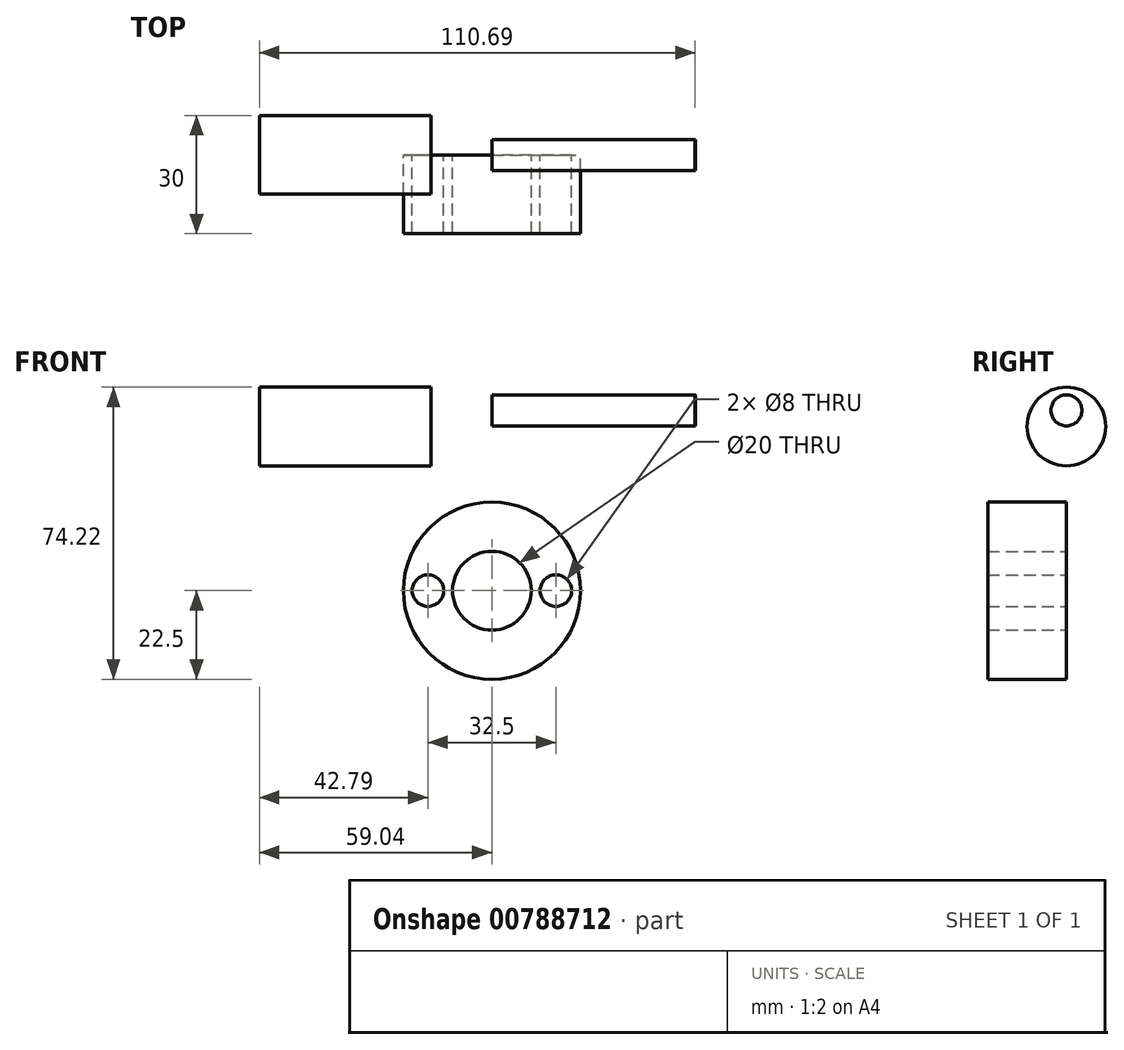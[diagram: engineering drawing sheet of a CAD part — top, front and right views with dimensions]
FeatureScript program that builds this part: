
annotation { "Feature Type Name" : "Feature", "Feature Type Description" : "" }
export const myFeature = defineFeature(function(context is Context, id is Id, definition is map)
    precondition{}
    {
        {
            var Q0;
            Q0=qCreatedBy(makeId("Front.planeOp"),FACE);
            var sketch = newSketch(context, id + "F0", { "sketchPlane" : qUnion([Q0])});
            skCircle(sketch, "E0", {"center": v(0, 0) * mm, "radius": 22.5 * mm});
            skCircle(sketch, "E1", {"center": v(0, 0) * mm, "radius": 10 * mm});
            skCircle(sketch, "E2", {"center": v(16.25, 0) * mm, "radius": 6.25 * mm});
            skCircle(sketch, "E3", {"center": v(-16.25, 0) * mm, "radius": 6.25 * mm});
            skCircle(sketch, "E4", {"center": v(-16.25, 0) * mm, "radius": 4 * mm});
            skCircle(sketch, "E5", {"center": v(16.25, 0) * mm, "radius": 4 * mm});
            skSolve(sketch);
        }
        {
            var Q0;
            {var subQ0=sQuery(id+"F0.wireOp",EDGE,"E2");var subQ1=sQuery(id+"F0.wireOp",EDGE,"E0");var subQ2=makeQuery(id+"F0.imprint","INTERSECT",VERTEX,{"derivedFrom":[subQ1,subQ0]});Q0=makeQuery(id+"F0.imprint","IMPRINT",FACE,{"disambiguationData":[TD([[makeQuery(id+"F0.imprint","IMPRINT",EDGE,{"disambiguationData":[TD([[subQ2,-1.0]])],"derivedFrom":subQ1}),1.0]])]});}
            var Q1;
            Q1=makeQuery(id+"F0.imprint","IMPRINT",FACE,{"disambiguationData":[TD([[makeQuery(id+"F0.imprint","IMPRINT",EDGE,{"derivedFrom":sQuery(id+"F0.wireOp",EDGE,"E5")}),-1.0]])]});
            var Q2;
            Q2=makeQuery(id+"F0.imprint","IMPRINT",FACE,{"disambiguationData":[TD([[makeQuery(id+"F0.imprint","IMPRINT",EDGE,{"derivedFrom":sQuery(id+"F0.wireOp",EDGE,"E4")}),-1.0]])]});
            var Q3;
            {var subQ0=sQuery(id+"F0.wireOp",EDGE,"E2");var subQ1=sQuery(id+"F0.wireOp",EDGE,"E0");var subQ2=makeQuery(id+"F0.imprint","INTERSECT",VERTEX,{"derivedFrom":[subQ1,subQ0]});Q3=makeQuery(id+"F0.imprint","IMPRINT",FACE,{"disambiguationData":[TD([[makeQuery(id+"F0.imprint","IMPRINT",EDGE,{"disambiguationData":[TD([[subQ2,1.0]])],"derivedFrom":subQ1}),1.0]])]});}
            extrude(context, id + "F1", {"entities" : qUnion([Q0, Q1, Q2, Q3]), "depth" : 20 * mm, "offsetDistance" : 25.4 * mm});
        }
        {
            var Q0;
            Q0=qCreatedBy(makeId("Front.planeOp"),FACE);
            var sketch = newSketch(context, id + "F2", { "sketchPlane" : qUnion([Q0])});
            skLineSegment(sketch, "E6.bottom", {"start": v(0, 49.73) * mm, "end": v(51.65, 49.73) * mm});
            skLineSegment(sketch, "E6.top", {"start": v(0, 45.8) * mm, "end": v(51.65, 45.8) * mm});
            skLineSegment(sketch, "E6.left", {"start": v(0, 49.73) * mm, "end": v(0, 45.8) * mm});
            skLineSegment(sketch, "E6.right", {"start": v(51.65, 49.73) * mm, "end": v(51.65, 45.8) * mm});
            skArc(sketch, "E7", {"start": v(51.65, 49.73) * mm, "mid": v(35.91, 53.93) * mm, "end": v(20.17, 49.73) * mm});
            skSolve(sketch);
        }
        {
            var Q0;
            {var subQ1=sQuery(id+"F2.wireOp",EDGE,"E6.top");Q0=makeQuery(id+"F2.imprint","IMPRINT",FACE,{"disambiguationData":[TD([[makeQuery(id+"F2.imprint","IMPRINT",EDGE,{"derivedFrom":subQ1}),1.0]])]});}
            var Q1;
            {var subQ0=sQuery(id+"F2.wireOp",EDGE,"E7");var subQ1=sQuery(id+"F2.wireOp",EDGE,"E6.bottom");var subQ2=makeQuery(id+"F2.imprint","INTERSECT",VERTEX,{"disambiguationData":[OD(0.0)],"derivedFrom":[subQ1,subQ0]});Q1=makeQuery(id+"F2.imprint","IMPRINT",FACE,{"disambiguationData":[TD([[makeQuery(id+"F2.imprint","IMPRINT",EDGE,{"disambiguationData":[TD([[subQ2,-1.0]])],"derivedFrom":subQ1}),1.0]])]});}
            var Q2;
            Q2=sQuery(id+"F2.wireOp",EDGE,"E6.top");
            revolve(context, id + "F3", {"surfaceOperationType" : NewSurfaceOperationType.NEW, "entities" : qUnion([Q0, Q1]), "axis" : qUnion([Q2]), "revolveType" : RevolveType.FULL});
        }
        {
            var Q0;
            Q0=qCreatedBy(makeId("Front.planeOp"),FACE);
            var sketch = newSketch(context, id + "F4", { "sketchPlane" : qUnion([Q0])});
            skLineSegment(sketch, "E8.bottom", {"start": v(-59.04, 41.72) * mm, "end": v(-15.45, 41.72) * mm});
            skLineSegment(sketch, "E8.top", {"start": v(-59.04, 31.72) * mm, "end": v(-15.45, 31.72) * mm});
            skLineSegment(sketch, "E8.left", {"start": v(-59.04, 41.72) * mm, "end": v(-59.04, 31.72) * mm});
            skLineSegment(sketch, "E8.right", {"start": v(-15.45, 41.72) * mm, "end": v(-15.45, 31.72) * mm});
            skSolve(sketch);
        }
        {
            var Q0;
            Q0=makeQuery(id+"F4.imprint","IMPRINT",FACE,{"disambiguationData":[TD([[makeQuery(id+"F4.imprint","IMPRINT",EDGE,{"derivedFrom":sQuery(id+"F4.wireOp",EDGE,"E8.bottom")}),-1.0]])]});
            var Q1;
            Q1=sQuery(id+"F4.wireOp",EDGE,"E8.bottom");
            revolve(context, id + "F5", {"surfaceOperationType" : NewSurfaceOperationType.NEW, "entities" : qUnion([Q0]), "axis" : qUnion([Q1]), "revolveType" : RevolveType.FULL});
        }
    });
